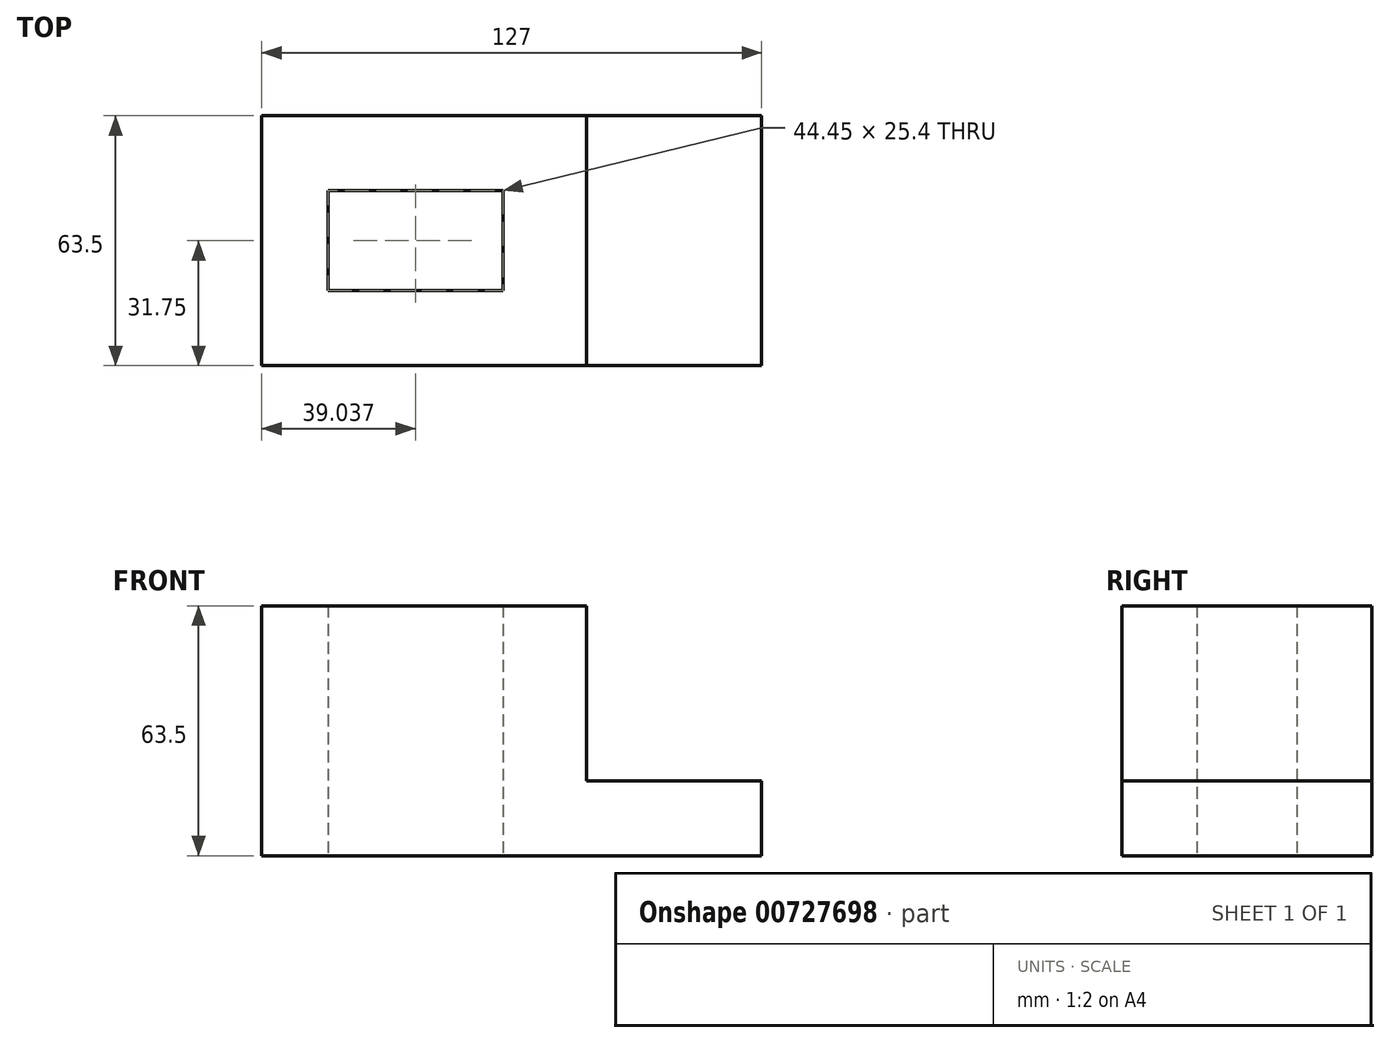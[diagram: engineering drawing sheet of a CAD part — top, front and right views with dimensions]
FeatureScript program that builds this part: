
annotation { "Feature Type Name" : "Feature", "Feature Type Description" : "" }
export const myFeature = defineFeature(function(context is Context, id is Id, definition is map)
    precondition{}
    {
        {
            var Q0;
            Q0=qCreatedBy(makeId("Top.planeOp"),FACE);
            var sketch = newSketch(context, id + "F0", { "sketchPlane" : qUnion([Q0])});
            skLineSegment(sketch, "E0", {"start": v(0, 0) * mm, "end": v(0, 63.5) * mm});
            skLineSegment(sketch, "E1", {"start": v(0, 63.5) * mm, "end": v(-82.55, 63.5) * mm});
            skLineSegment(sketch, "E2", {"start": v(-82.55, 63.5) * mm, "end": v(-82.55, 0) * mm});
            skLineSegment(sketch, "E3", {"start": v(-82.55, 0) * mm, "end": v(0, 0) * mm});
            skLineSegment(sketch, "E4", {"start": v(-21.29, 44.45) * mm, "end": v(-21.29, 19.05) * mm});
            skLineSegment(sketch, "E5", {"start": v(-21.29, 19.05) * mm, "end": v(-65.74, 19.05) * mm});
            skLineSegment(sketch, "E6", {"start": v(-65.74, 19.05) * mm, "end": v(-65.74, 44.45) * mm});
            skLineSegment(sketch, "E7", {"start": v(-65.74, 44.45) * mm, "end": v(-21.29, 44.45) * mm});
            skSolve(sketch);
        }
        {
            var Q0;
            Q0=qCreatedBy(makeId("Top.planeOp"),FACE);
            var sketch = newSketch(context, id + "F1", { "sketchPlane" : qUnion([Q0])});
            skLineSegment(sketch, "E8", {"start": v(0, 0) * mm, "end": v(44.45, 0) * mm});
            skLineSegment(sketch, "E9", {"start": v(44.45, 0) * mm, "end": v(44.45, 63.5) * mm});
            skLineSegment(sketch, "E10", {"start": v(44.45, 63.5) * mm, "end": v(0, 63.5) * mm});
            skLineSegment(sketch, "E11", {"start": v(0, 63.5) * mm, "end": v(0, 0) * mm});
            skSolve(sketch);
        }
        {
            var Q0;
            Q0 = qSketchRegion(id + "F0", true);
            extrude(context, id + "F2", {"entities" : qUnion([Q0]), "depth" : 63.5 * mm, "offsetDistance" : 25.4 * mm});
        }
        {
            var Q0;
            Q0 = qSketchRegion(id + "F1", true);
            extrude(context, id + "F3", {"entities" : qUnion([Q0]), "operationType" : NewBodyOperationType.ADD, "depth" : 19.05 * mm, "offsetDistance" : 25.4 * mm});
        }
    });
